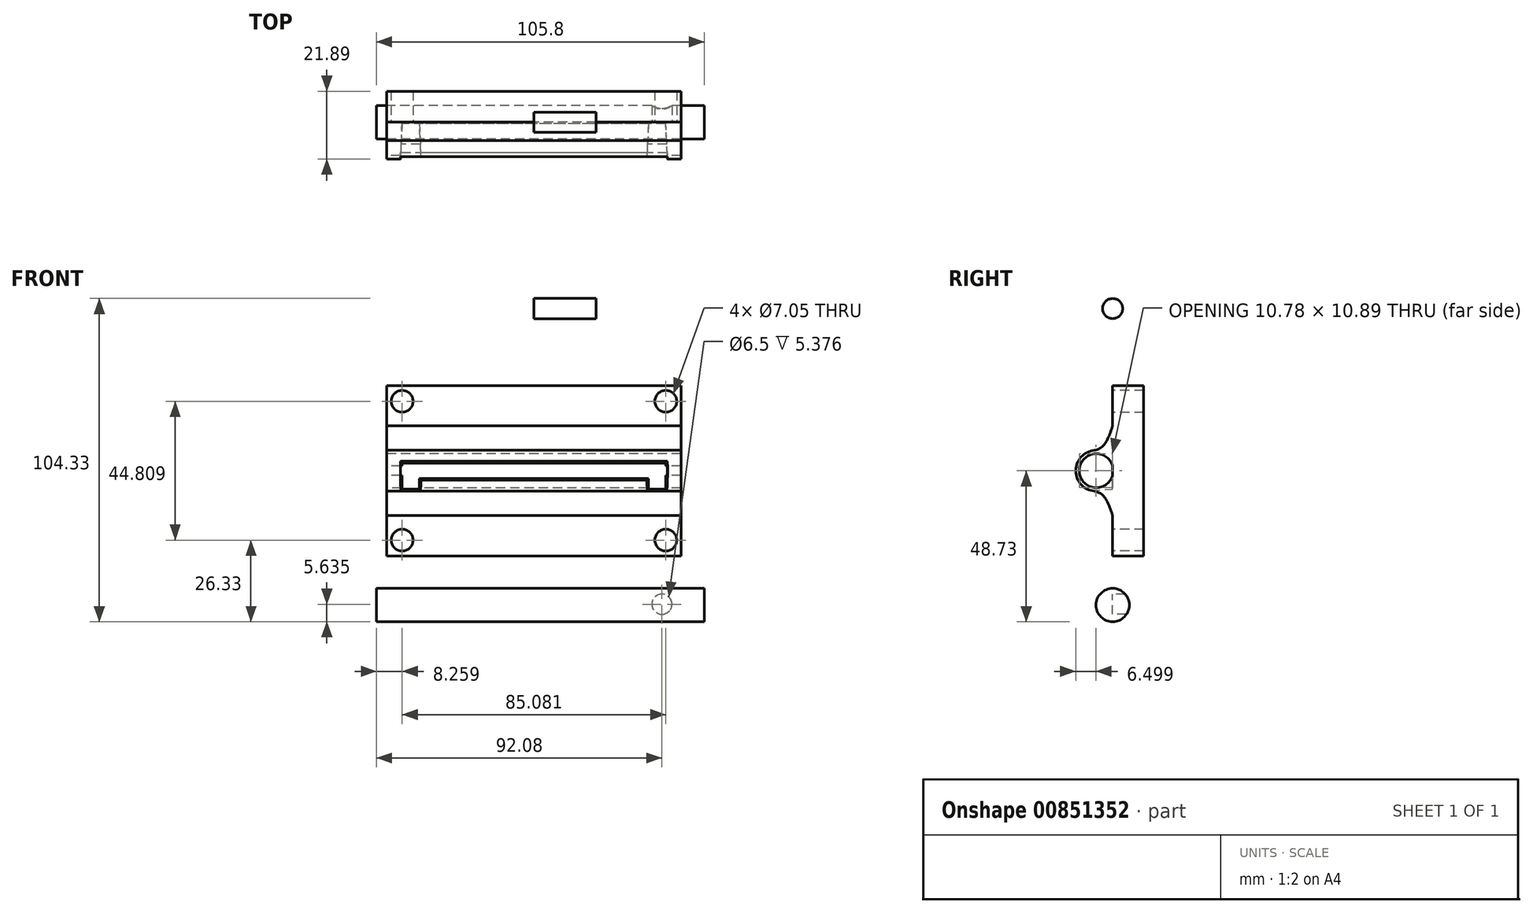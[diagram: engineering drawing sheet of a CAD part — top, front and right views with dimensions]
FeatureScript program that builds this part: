
annotation { "Feature Type Name" : "Feature", "Feature Type Description" : "" }
export const myFeature = defineFeature(function(context is Context, id is Id, definition is map)
    precondition{}
    {
        {
            var Q0;
            Q0=qCreatedBy(makeId("Front.planeOp"),FACE);
            var sketch = newSketch(context, id + "F0", { "sketchPlane" : qUnion([Q0])});
            skLineSegment(sketch, "E0.bottom", {"start": v(47.5, -27.5) * mm, "end": v(-47.5, -27.5) * mm});
            skLineSegment(sketch, "E0.top", {"start": v(47.5, 27.5) * mm, "end": v(-47.5, 27.5) * mm});
            skLineSegment(sketch, "E0.left", {"start": v(47.5, -27.5) * mm, "end": v(47.5, 27.5) * mm});
            skLineSegment(sketch, "E0.right", {"start": v(-47.5, -27.5) * mm, "end": v(-47.5, 27.5) * mm});
            skPoint(sketch, "E0.middle", {"position": v(0, 0) * mm});
            skLineSegment(sketch, "E1", {"start": v(0, 27.5) * mm, "end": v(0, -27.5) * mm});
            skCircle(sketch, "E2", {"center": v(-42.54, 22.4) * mm, "radius": 3.52 * mm});
            skCircle(sketch, "E3", {"center": v(-42.54, -22.4) * mm, "radius": 3.52 * mm});
            skCircle(sketch, "E4.MirrorC", {"center": v(42.54, -22.4) * mm, "radius": 3.52 * mm});
            skCircle(sketch, "E5.MirrorC", {"center": v(42.54, 22.4) * mm, "radius": 3.52 * mm});
            skSolve(sketch);
        }
        {
            var Q0;
            Q0=qCreatedBy(makeId("Right.planeOp"),FACE);
            var sketch = newSketch(context, id + "F1", { "sketchPlane" : qUnion([Q0])});
            skCircle(sketch, "E6", {"center": v(-5.28, 0) * mm, "radius": 6.61 * mm});
            skFitSpline(sketch, "E7", {"points": [v(-6.6, -6.44) * mm, v(-3.08, -8.02) * mm, v(0, -14.54) * mm], "startDerivative": vector(9.4, -1.6) * mm, "endDerivative": vector(4.41, -13.66) * mm});
            skFitSpline(sketch, "E8.MirrorCS", {"points": [v(-6.6, 6.44) * mm, v(-3.08, 8.02) * mm, v(0, 14.54) * mm], "startDerivative": vector(9.4, 1.6) * mm, "endDerivative": vector(4.41, 13.66) * mm});
            skLineSegment(sketch, "E9", {"start": v(0, 14.54) * mm, "end": v(0, -14.54) * mm});
            skLineSegment(sketch, "E10.bottom", {"start": v(0, 14.54) * mm, "end": v(-12.1, 14.54) * mm});
            skLineSegment(sketch, "E10.top", {"start": v(0, -14.5) * mm, "end": v(-12.1, -14.5) * mm});
            skLineSegment(sketch, "E10.left", {"start": v(0, 14.54) * mm, "end": v(0, -14.5) * mm});
            skLineSegment(sketch, "E10.right", {"start": v(-12.1, 14.54) * mm, "end": v(-12.1, -14.5) * mm});
            skCircle(sketch, "E11", {"center": v(-5.28, 0) * mm, "radius": 5.5 * mm});
            skSolve(sketch);
        }
        {
            var Q0;
            {var subQ0=sQuery(id+"F0.wireOp",EDGE,"E0.right");Q0=makeQuery(id+"F0.imprint","IMPRINT",FACE,{"disambiguationData":[TD([[makeQuery(id+"F0.imprint","IMPRINT",EDGE,{"derivedFrom":subQ0}),-1.0]])]});}
            var Q1;
            {var subQ1=sQuery(id+"F0.wireOp",EDGE,"E0.left");Q1=makeQuery(id+"F0.imprint","IMPRINT",FACE,{"disambiguationData":[TD([[makeQuery(id+"F0.imprint","IMPRINT",EDGE,{"derivedFrom":subQ1}),1.0]])]});}
            extrude(context, id + "F2", {"entities" : qUnion([Q0, Q1]), "depth" : -10 * mm, "offsetDistance" : 25 * mm});
        }
        {
            var Q0;
            {var subQ0=sQuery(id+"F1.wireOp",EDGE,"E10.left");var subQ1=sQuery(id+"F1.wireOp",EDGE,"E6");var subQ2=makeQuery(id+"F1.imprint","INTERSECT",VERTEX,{"disambiguationData":[OD(0.0)],"derivedFrom":[subQ1,subQ0]});Q0=makeQuery(id+"F1.imprint","IMPRINT",FACE,{"disambiguationData":[TD([[makeQuery(id+"F1.imprint","IMPRINT",EDGE,{"disambiguationData":[TD([[subQ2,1.0]])],"derivedFrom":subQ1}),1.0]])]});}
            var Q1;
            {var subQ0=sQuery(id+"F1.wireOp",EDGE,"E9");Q1=makeQuery(id+"F1.imprint","IMPRINT",FACE,{"disambiguationData":[TD([[makeQuery(id+"F1.imprint","IMPRINT",EDGE,{"derivedFrom":subQ0}),-1.0]])]});}
            var Q2;
            {var subQ0=sQuery(id+"F1.wireOp",EDGE,"E7");var subQ1=sQuery(id+"F1.wireOp",EDGE,"E6");var subQ2=makeQuery(id+"F1.imprint","INTERSECT",VERTEX,{"derivedFrom":[subQ1,subQ0]});Q2=makeQuery(id+"F1.imprint","IMPRINT",FACE,{"disambiguationData":[TD([[makeQuery(id+"F1.imprint","IMPRINT",EDGE,{"disambiguationData":[TD([[subQ2,-1.0]])],"derivedFrom":subQ1}),-1.0]])]});}
            var Q3;
            {var subQ0=sQuery(id+"F1.wireOp",EDGE,"E6");var subQ1=makeQuery(id+"F1.imprint","INTERSECT",VERTEX,{"derivedFrom":[subQ0,sQuery(id+"F1.wireOp",EDGE,"E8.MirrorCS")]});Q3=makeQuery(id+"F1.imprint","IMPRINT",FACE,{"disambiguationData":[TD([[makeQuery(id+"F1.imprint","IMPRINT",EDGE,{"disambiguationData":[TD([[subQ1,1.0]])],"derivedFrom":subQ0}),1.0]])]});}
            var Q4;
            {var subQ0=sQuery(id+"F1.wireOp",EDGE,"E8.MirrorCS");var subQ1=sQuery(id+"F1.wireOp",EDGE,"E6");var subQ2=makeQuery(id+"F1.imprint","INTERSECT",VERTEX,{"derivedFrom":[subQ1,subQ0]});Q4=makeQuery(id+"F1.imprint","IMPRINT",FACE,{"disambiguationData":[TD([[makeQuery(id+"F1.imprint","IMPRINT",EDGE,{"disambiguationData":[TD([[subQ2,1.0]])],"derivedFrom":subQ1}),-1.0]])]});}
            extrude(context, id + "F3", {"entities" : qUnion([Q0, Q1, Q2, Q3, Q4]), "operationType" : NewBodyOperationType.ADD, "depth" : 47.5 * mm, "offsetDistance" : 25 * mm});
        }
        {
            var Q0;
            Q0=makeQuery(id+"F3.opExtrude","CAP_FACE",FACE,{"disambiguationData":[OSD([sQuery(id+"F1.wireOp",EDGE,"E6"),sQuery(id+"F1.wireOp",EDGE,"E7"),sQuery(id+"F1.wireOp",EDGE,"E8.MirrorCS"),sQuery(id+"F1.wireOp",EDGE,"E9"),sQuery(id+"F1.wireOp",EDGE,"E10.left")])],"isStart":true});
            extrude(context, id + "F4", {"entities" : qUnion([Q0]), "operationType" : NewBodyOperationType.ADD, "depth" : 47.5 * mm, "offsetDistance" : 25 * mm});
        }
        {
            var Q0;
            Q0=qCreatedBy(makeId("Front.planeOp"),FACE);
            var sketch = newSketch(context, id + "F5", { "sketchPlane" : qUnion([Q0])});
            skLineSegment(sketch, "E12.bottom", {"start": v(42.5, -2.5) * mm, "end": v(-42.5, -2.5) * mm});
            skLineSegment(sketch, "E12.top", {"start": v(42.5, 2.5) * mm, "end": v(-42.5, 2.5) * mm});
            skLineSegment(sketch, "E12.left", {"start": v(42.5, -2.5) * mm, "end": v(42.5, 2.5) * mm});
            skLineSegment(sketch, "E12.right", {"start": v(-42.5, -2.5) * mm, "end": v(-42.5, 2.5) * mm});
            skPoint(sketch, "E12.middle", {"position": v(0, 0) * mm});
            skLineSegment(sketch, "E13.bottom", {"start": v(-42.5, -2.5) * mm, "end": v(-37, -2.5) * mm});
            skLineSegment(sketch, "E13.top", {"start": v(-42.5, -6) * mm, "end": v(-37, -6) * mm});
            skLineSegment(sketch, "E13.left", {"start": v(-42.5, -2.5) * mm, "end": v(-42.5, -6) * mm});
            skLineSegment(sketch, "E13.right", {"start": v(-37, -2.5) * mm, "end": v(-37, -6) * mm});
            skLineSegment(sketch, "E14.bottom", {"start": v(42.5, -2.5) * mm, "end": v(37, -2.5) * mm});
            skLineSegment(sketch, "E14.top", {"start": v(42.5, -6) * mm, "end": v(37, -6) * mm});
            skLineSegment(sketch, "E14.left", {"start": v(42.5, -2.5) * mm, "end": v(42.5, -6) * mm});
            skLineSegment(sketch, "E14.right", {"start": v(37, -2.5) * mm, "end": v(37, -6) * mm});
            skSolve(sketch);
        }
        {
            var Q0;
            {Q0=qUnion([makeQuery(id+"F5.imprint","IMPRINT",FACE,{"disambiguationData":[TD([[makeQuery(id+"F5.imprint","IMPRINT",EDGE,{"derivedFrom":sQuery(id+"F5.wireOp",EDGE,"E13.top")}),1.0]])]}),makeQuery(id+"F5.imprint","IMPRINT",FACE,{"disambiguationData":[TD([[makeQuery(id+"F5.imprint","IMPRINT",EDGE,{"derivedFrom":sQuery(id+"F5.wireOp",EDGE,"E14.top")}),-1.0]])]}),makeQuery(id+"F5.imprint","IMPRINT",FACE,{"disambiguationData":[TD([[makeQuery(id+"F5.imprint","IMPRINT",EDGE,{"derivedFrom":sQuery(id+"F5.wireOp",EDGE,"E12.top")}),1.0]])]})]);}
            var Q1;
            {var subQ0=sQuery(id+"F1.wireOp",EDGE,"E6");Q1=makeQuery(id+"F4.boolean.opBoolean","MERGE",FACE,{"derivedFrom":[makeQuery(id+"F3.opExtrude","SWEPT_FACE",FACE,{"disambiguationData":[OSD([subQ0]),TDD([makeQuery(id+"F1.imprint","IMPRINT",EDGE,{"disambiguationData":[TD([[makeQuery(id+"F1.imprint","INTERSECT",VERTEX,{"derivedFrom":[subQ0,sQuery(id+"F1.wireOp",EDGE,"E8.MirrorCS")]}),-1.0]])],"derivedFrom":subQ0})])]}),makeQuery(id+"F4.opExtrude","SWEPT_FACE",FACE,{"disambiguationData":[OSD([subQ0])]})]});}
            extrude(context, id + "F6", {"entities" : qUnion([Q0]), "operationType" : NewBodyOperationType.REMOVE, "endBound" : BoundingType.UP_TO_SURFACE, "depth" : 25 * mm, "endBoundEntityFace" : qUnion([Q1]), "offsetDistance" : 25 * mm, "hasDraft" : true, "draftAngle" : 3 * degree});
        }
        {
            var Q0;
            Q0=qCreatedBy(makeId("Right.planeOp"),FACE);
            var sketch = newSketch(context, id + "F7", { "sketchPlane" : qUnion([Q0])});
            skCircle(sketch, "E15", {"center": v(0, -43.36) * mm, "radius": 5.38 * mm});
            skSolve(sketch);
        }
        {
            var Q0;
            Q0=makeQuery(id+"F7.imprint","IMPRINT",FACE,{"disambiguationData":[TD([[makeQuery(id+"F7.imprint","IMPRINT",EDGE,{"derivedFrom":sQuery(id+"F7.wireOp",EDGE,"E15")}),1.0]])]});
            extrude(context, id + "F8", {"entities" : qUnion([Q0]), "depth" : 55 * mm, "offsetDistance" : 25 * mm});
        }
        {
            var Q0;
            Q0=makeQuery(id+"F8.opExtrude","CAP_FACE",FACE,{"disambiguationData":[OSD([sQuery(id+"F7.wireOp",EDGE,"E15")])],"isStart":true});
            extrude(context, id + "F9", {"entities" : qUnion([Q0]), "operationType" : NewBodyOperationType.ADD, "depth" : 50.8 * mm, "offsetDistance" : 25 * mm});
        }
        {
            var Q0;
            Q0=qCreatedBy(makeId("Front.planeOp"),FACE);
            var sketch = newSketch(context, id + "F10", { "sketchPlane" : qUnion([Q0])});
            skCircle(sketch, "E16", {"center": v(41.28, -43.1) * mm, "radius": 3.25 * mm});
            skSolve(sketch);
        }
        {
            var Q0;
            Q0 = qSketchRegion(id + "F10", true);
            extrude(context, id + "F11", {"entities" : qUnion([Q0]), "operationType" : NewBodyOperationType.REMOVE, "oppositeDirection" : true, "depth" : 25 * mm, "offsetDistance" : 25 * mm});
        }
        {
            var Q0;
            Q0=qCreatedBy(makeId("Right.planeOp"),FACE);
            var sketch = newSketch(context, id + "F12", { "sketchPlane" : qUnion([Q0])});
            skCircle(sketch, "E17", {"center": v(0, 52.35) * mm, "radius": 3.25 * mm});
            skSolve(sketch);
        }
        {
            var Q0;
            Q0=makeQuery(id+"F12.imprint","IMPRINT",FACE,{"disambiguationData":[TD([[makeQuery(id+"F12.imprint","IMPRINT",EDGE,{"derivedFrom":sQuery(id+"F12.wireOp",EDGE,"E17")}),1.0]])]});
            var Q1;
            Q1=sQuery(id+"F12.wireOp",EDGE,"E17");
            extrude(context, id + "F13", {"entities" : qUnion([Q0]), "surfaceEntities" : qUnion([Q1]), "depth" : 20 * mm, "offsetDistance" : 25 * mm});
        }
    });
